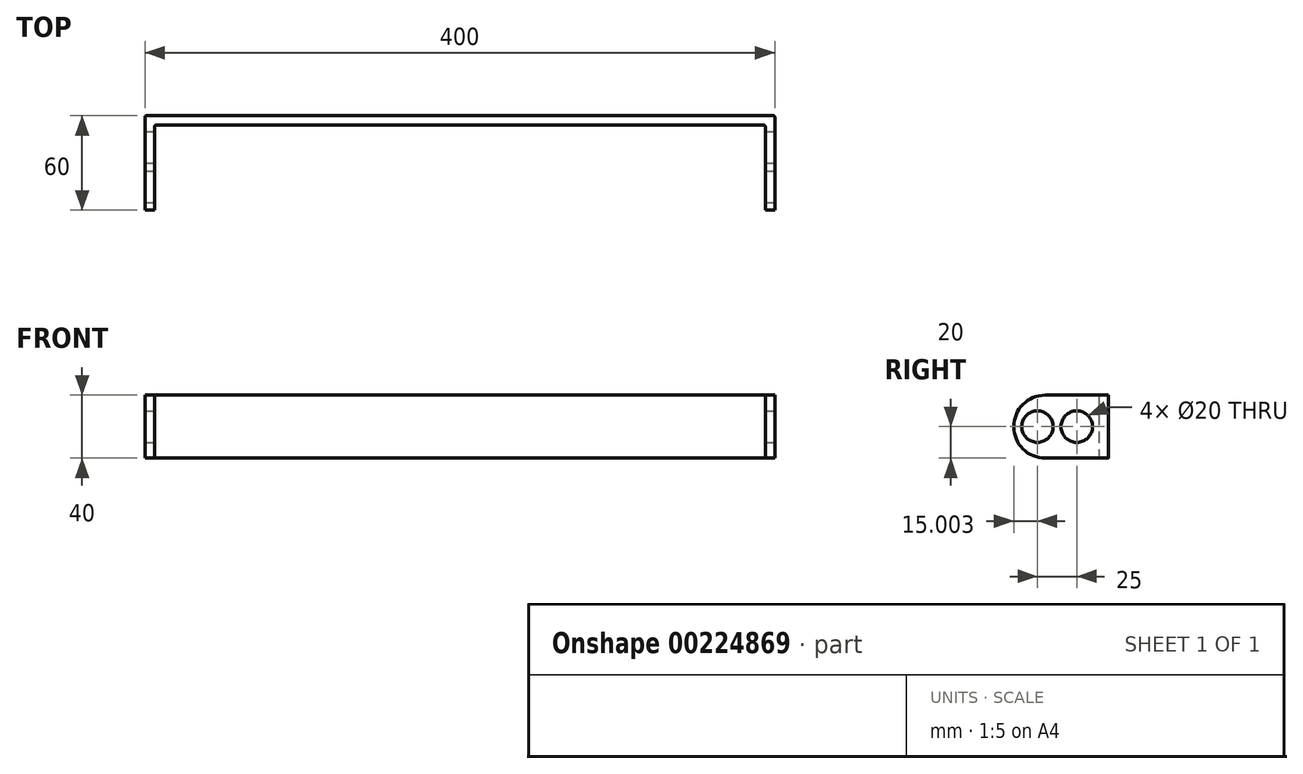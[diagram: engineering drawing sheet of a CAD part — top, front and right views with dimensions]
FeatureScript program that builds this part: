
annotation { "Feature Type Name" : "Feature", "Feature Type Description" : "" }
export const myFeature = defineFeature(function(context is Context, id is Id, definition is map)
    precondition{}
    {
        {
            var Q0;
            Q0=qCreatedBy(makeId("Top.planeOp"),FACE);
            var sketch = newSketch(context, id + "F0", { "sketchPlane" : qUnion([Q0])});
            skLineSegment(sketch, "E0", {"start": v(-195.68, 14.57) * mm, "end": v(202.32, 14.57) * mm});
            skLineSegment(sketch, "E1", {"start": v(203.32, 13.57) * mm, "end": v(203.32, -45.43) * mm});
            skLineSegment(sketch, "E2.0", {"start": v(-189.68, 8.57) * mm, "end": v(196.32, 8.57) * mm});
            skLineSegment(sketch, "E3.0", {"start": v(197.32, 7.57) * mm, "end": v(197.32, -45.43) * mm});
            skLineSegment(sketch, "E4", {"start": v(-196.68, 13.57) * mm, "end": v(-196.68, -45.43) * mm});
            skLineSegment(sketch, "E5.0", {"start": v(-190.68, 7.57) * mm, "end": v(-190.68, -45.43) * mm});
            skLineSegment(sketch, "E6", {"start": v(-196.68, -45.43) * mm, "end": v(-190.68, -45.43) * mm});
            skLineSegment(sketch, "E7", {"start": v(197.32, -45.43) * mm, "end": v(203.32, -45.43) * mm});
            skPoint(sketch, "E8.visualSharp", {"position": v(-196.68, 14.57) * mm});
            skArc(sketch, "E8.filletArc", {"start": v(-195.68, 14.57) * mm, "mid": v(-196.4, 14.28) * mm, "end": v(-196.68, 13.57) * mm});
            skPoint(sketch, "E9.visualSharp", {"position": v(-190.68, 8.57) * mm});
            skArc(sketch, "E9.filletArc", {"start": v(-189.68, 8.57) * mm, "mid": v(-190.4, 8.28) * mm, "end": v(-190.68, 7.57) * mm});
            skPoint(sketch, "E10.visualSharp", {"position": v(203.32, 14.57) * mm});
            skArc(sketch, "E10.filletArc", {"start": v(203.32, 13.57) * mm, "mid": v(203.02, 14.28) * mm, "end": v(202.32, 14.57) * mm});
            skPoint(sketch, "E11.visualSharp", {"position": v(197.32, 8.57) * mm});
            skArc(sketch, "E11.filletArc", {"start": v(197.32, 7.57) * mm, "mid": v(197.02, 8.28) * mm, "end": v(196.32, 8.57) * mm});
            skSolve(sketch);
        }
        {
            var Q0;
            Q0 = qSketchRegion(id + "F0", true);
            extrude(context, id + "F1", {"entities" : qUnion([Q0]), "depth" : 40 * mm});
        }
        {
            var Q0;
            Q0=makeQuery(id+"F1.opExtrude","SWEPT_FACE",FACE,{"disambiguationData":[OSD([sQuery(id+"F0.wireOp",EDGE,"E1")])]});
            var sketch = newSketch(context, id + "F2", { "sketchPlane" : qUnion([Q0])});
            skLineSegment(sketch, "E12", {"start": v(-66.18, 59.7) * mm, "end": v(-66.18, -19.47) * mm});
            skLineSegment(sketch, "E13", {"start": v(-66.18, -19.47) * mm, "end": v(-23.14, -19.47) * mm});
            skLineSegment(sketch, "E14", {"start": v(-23.14, -19.47) * mm, "end": v(-23.14, 0) * mm});
            skLineSegment(sketch, "E15", {"start": v(-23.14, 0) * mm, "end": v(-25.43, 0) * mm});
            skLineSegment(sketch, "E16", {"start": v(-45.43, 20) * mm, "end": v(-45.43, 20) * mm});
            skLineSegment(sketch, "E17", {"start": v(-25.43, 40) * mm, "end": v(-23.14, 40) * mm});
            skLineSegment(sketch, "E18", {"start": v(-23.14, 40) * mm, "end": v(-23.14, 59.7) * mm});
            skLineSegment(sketch, "E19", {"start": v(-23.14, 59.7) * mm, "end": v(-66.18, 59.7) * mm});
            skPoint(sketch, "E20.visualSharp", {"position": v(-45.43, 40) * mm});
            skArc(sketch, "E20.filletArc", {"start": v(-25.43, 40) * mm, "mid": v(-39.57, 34.14) * mm, "end": v(-45.43, 20) * mm});
            skPoint(sketch, "E21.visualSharp", {"position": v(-45.43, 0) * mm});
            skArc(sketch, "E21.filletArc", {"start": v(-45.43, 20) * mm, "mid": v(-39.57, 5.86) * mm, "end": v(-25.43, 0) * mm});
            skLineSegment(sketch, "E22", {"start": v(-45.43, 20) * mm, "end": v(28.37, 20) * mm, "construction": true});
            skCircle(sketch, "E23", {"center": v(-30.43, 20) * mm, "radius": 10 * mm});
            skCircle(sketch, "E24", {"center": v(-5.43, 20) * mm, "radius": 10 * mm});
            skSolve(sketch);
        }
        {
            var Q0;
            Q0 = qSketchRegion(id + "F2", true);
            extrude(context, id + "F3", {"entities" : qUnion([Q0]), "operationType" : NewBodyOperationType.REMOVE, "endBound" : BoundingType.THROUGH_ALL, "oppositeDirection" : true, "depth" : 25 * mm});
        }
    });
